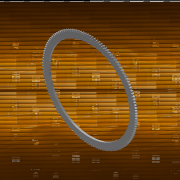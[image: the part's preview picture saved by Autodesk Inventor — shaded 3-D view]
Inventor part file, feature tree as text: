
AUTODESK INVENTOR PART (.ipt)
format: ipt  version: 2017 (Build 210142000, 142)  size: 690,688 bytes
history: native  units: mm (DEFAULTED — no unit token found)
features: plane x3, other x3, sketch x3, extrude x2
ambient origin geometry x8: Origin, YZ Plane, XZ Plane, XY Plane, X Axis, Y Axis, Z Axis, Center Point
bodies: Solid1 (feature_tree)
feature tree (11):
  extrude  "Extrusion1"  Depth=6.35mm TaperAngle=0.0deg
  plane  "Work Plane1"
  plane  "Work Plane2"
  plane  "Work Plane3"
  other  "Spur Gear"
  extrude  "Extrusion2"  Depth=76.2mm TaperAngle=0.0deg
  sketch  "Sketch1"  dims[d0=330.2mm d1=6.35mm d2=0.0mm]
  sketch  "Sketch2"  dims[d3=325.12mm d4=76.2mm d5=0.0mm]
  other  "Srf1"
  sketch  "Sketch3"  dims[d6=0.0mm d7=0.245437mm d9=0.0mm d14=0.0mm d15=181.61mm d16=0.0mm d17=0.0mm d18=0.0mm d19=181.61mm d20=282.575mm d21=25.4mm d22=0.0mm]
  other  "Pitch Diameter"
